# Revit family: EOS1.0-P-DI
name_source: partatom
category: Lighting Fixtures
revit_build: Autodesk Revit 2018 (Build: 20170223_1515(x64)
units: mm (PartAtom-declared; Revit-internal decimal feet)

## family parameters
Cut with Voids When Loaded = No
Host = Face
Light Source = Yes
Part Type = Normal
Room Calculation Point = Yes
Round Connector Dimension = Use Diameter
Shared = Yes

## types (7) — shared parameters
Color Filter = 16777215
Default Elevation = 4' - 0"
Dimming Lamp Color Temperature Shift = <None>
Emit Shape Visible in Rendering = Yes
Emit from Rectangle Width = 0' - 1 7/16"
Fixture Symbol Visiblity = Yes
Fixture Width = 0' - 1 11/16"
Lamp = LED
Photometric Web File = EOS1.0-P-DI-375-375-4-40K-8-1-UNV-S1.ies
Switch Leg Visibility = No
Tilt Angle = 90.00°
Voltage = 0 V

## per-type parameters (varying)
| type | Apparent Load | Emit from Rectangle Length | Fixture Length |
| 2' Direct/ Indirect | 31 VA | 2' - 0" | 2' - 0" |
| 3' Direct/ Indirect | 23 VA | 3' - 0" | 3' - 0" |
| 4' Direct/ Indirect | 31 VA | 4' - 0" | 4' - 0" |
| 5' Direct/ Indirect | 38 VA | 5' - 0" | 5' - 0" |
| 6' Direct/ Indirect | 46 VA | 6' - 0" | 6' - 0" |
| 7' Direct/ Indirect | 54 VA | 7' - 0" | 7' - 0" |
| 8' Direct/ Indirect | 61 VA | 8' - 0" | 8' - 0" |

## geometry (parser evidence)
native form markers: Sweep x9
no freeform markers — native parametric forms only
